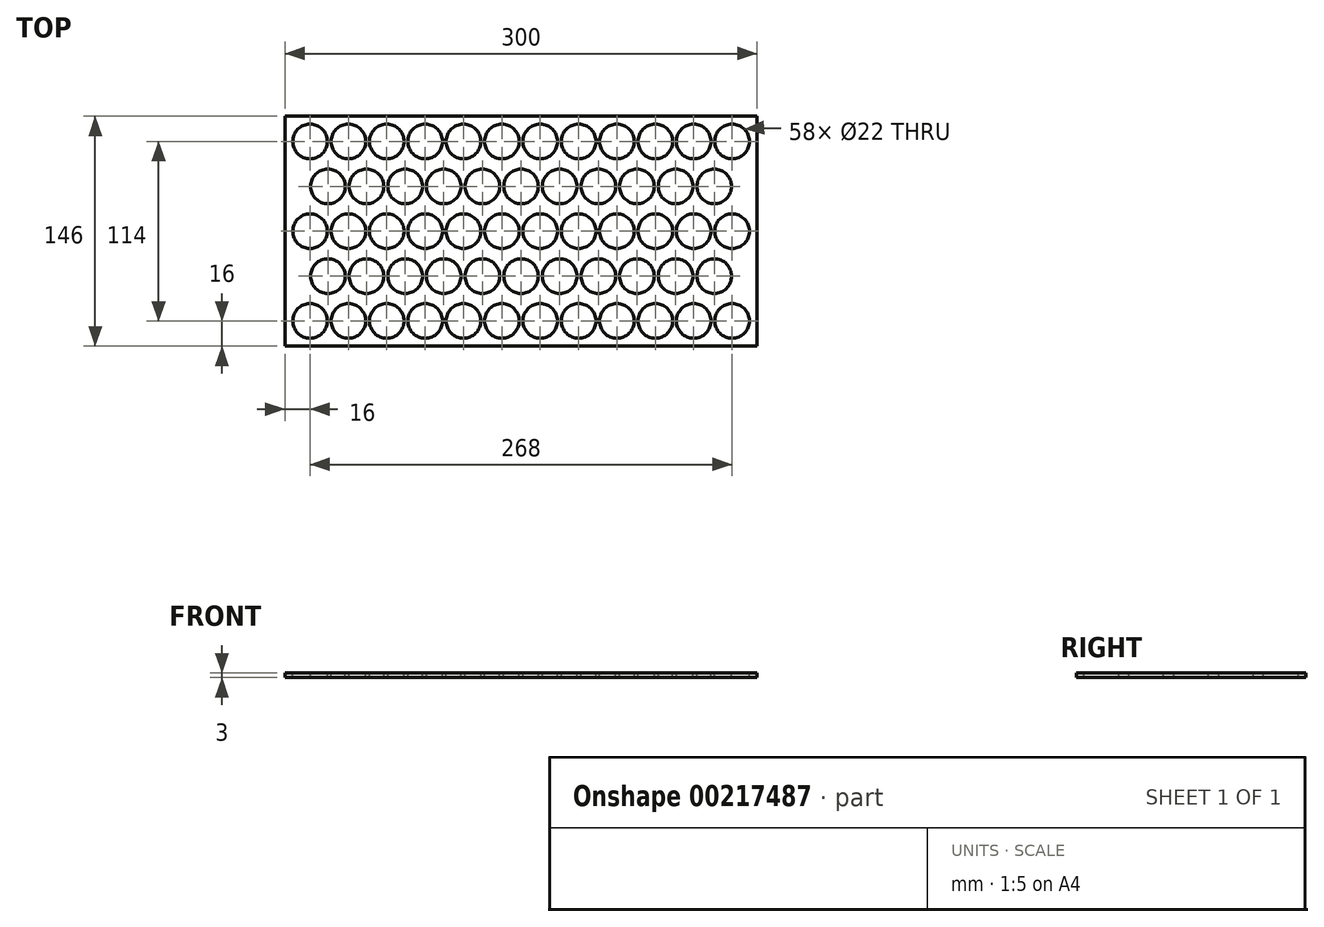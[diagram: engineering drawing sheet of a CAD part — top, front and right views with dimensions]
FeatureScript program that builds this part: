
annotation { "Feature Type Name" : "Feature", "Feature Type Description" : "" }
export const myFeature = defineFeature(function(context is Context, id is Id, definition is map)
    precondition{}
    {
        {
            var Q0;
            Q0=qCreatedBy(makeId("Top.planeOp"),FACE);
            var sketch = newSketch(context, id + "F0", { "sketchPlane" : qUnion([Q0])});
            skLineSegment(sketch, "E0.bottom", {"start": v(0, 0) * mm, "end": v(300, 0) * mm});
            skLineSegment(sketch, "E0.top", {"start": v(0, 146) * mm, "end": v(300, 146) * mm});
            skLineSegment(sketch, "E0.left", {"start": v(0, 0) * mm, "end": v(0, 146) * mm});
            skLineSegment(sketch, "E0.right", {"start": v(300, 0) * mm, "end": v(300, 146) * mm});
            skSolve(sketch);
        }
        {
            var Q0;
            Q0=makeQuery(id+"F0.imprint","IMPRINT",FACE,{"disambiguationData":[TD([[makeQuery(id+"F0.imprint","IMPRINT",EDGE,{"derivedFrom":sQuery(id+"F0.wireOp",EDGE,"E0.bottom")}),1.0]])]});
            extrude(context, id + "F1", {"entities" : qUnion([Q0]), "depth" : 3 * mm});
        }
        {
            var Q0;
            Q0=makeQuery(id+"F1.opExtrude","CAP_FACE",FACE,{"disambiguationData":[OSD([sQuery(id+"F0.wireOp",EDGE,"E0.bottom"),sQuery(id+"F0.wireOp",EDGE,"E0.top"),sQuery(id+"F0.wireOp",EDGE,"E0.left"),sQuery(id+"F0.wireOp",EDGE,"E0.right")])],"isStart":false});
            var sketch = newSketch(context, id + "F2", { "sketchPlane" : qUnion([Q0])});
            skCircle(sketch, "E1", {"center": v(16, 130) * mm, "radius": 11 * mm});
            skCircle(sketch, "E2.1.0.0", {"center": v(40.36, 130) * mm, "radius": 11 * mm});
            skCircle(sketch, "E2.2.0.0", {"center": v(64.73, 130) * mm, "radius": 11 * mm});
            skCircle(sketch, "E2.3.0.0", {"center": v(89.1, 130) * mm, "radius": 11 * mm});
            skCircle(sketch, "E2.4.0.0", {"center": v(113.45, 130) * mm, "radius": 11 * mm});
            skCircle(sketch, "E2.5.0.0", {"center": v(137.82, 130) * mm, "radius": 11 * mm});
            skCircle(sketch, "E2.6.0.0", {"center": v(162.18, 130) * mm, "radius": 11 * mm});
            skCircle(sketch, "E2.7.0.0", {"center": v(186.55, 130) * mm, "radius": 11 * mm});
            skCircle(sketch, "E2.8.0.0", {"center": v(210.9, 130) * mm, "radius": 11 * mm});
            skCircle(sketch, "E2.9.0.0", {"center": v(235.27, 130) * mm, "radius": 11 * mm});
            skCircle(sketch, "E2.10.0.0", {"center": v(259.64, 130) * mm, "radius": 11 * mm});
            skCircle(sketch, "E2.11.0.0", {"center": v(284, 130) * mm, "radius": 11 * mm});
            skLineSegment(sketch, "E2.direction1", {"start": v(16, 130) * mm, "end": v(40.36, 130) * mm, "construction": true});
            skCircle(sketch, "E3.0.1.0", {"center": v(16, 73) * mm, "radius": 11 * mm});
            skCircle(sketch, "E3.0.1.1", {"center": v(40.36, 73) * mm, "radius": 11 * mm});
            skCircle(sketch, "E3.0.1.2", {"center": v(64.73, 73) * mm, "radius": 11 * mm});
            skCircle(sketch, "E3.0.1.3", {"center": v(89.1, 73) * mm, "radius": 11 * mm});
            skCircle(sketch, "E3.0.1.4", {"center": v(113.45, 73) * mm, "radius": 11 * mm});
            skCircle(sketch, "E3.0.1.5", {"center": v(137.82, 73) * mm, "radius": 11 * mm});
            skCircle(sketch, "E3.0.1.6", {"center": v(162.18, 73) * mm, "radius": 11 * mm});
            skCircle(sketch, "E3.0.1.7", {"center": v(186.55, 73) * mm, "radius": 11 * mm});
            skCircle(sketch, "E3.0.1.8", {"center": v(210.9, 73) * mm, "radius": 11 * mm});
            skCircle(sketch, "E3.0.1.9", {"center": v(235.27, 73) * mm, "radius": 11 * mm});
            skCircle(sketch, "E3.0.1.10", {"center": v(259.64, 73) * mm, "radius": 11 * mm});
            skCircle(sketch, "E3.0.1.11", {"center": v(284, 73) * mm, "radius": 11 * mm});
            skCircle(sketch, "E3.0.2.0", {"center": v(16, 16) * mm, "radius": 11 * mm});
            skCircle(sketch, "E3.0.2.1", {"center": v(40.36, 16) * mm, "radius": 11 * mm});
            skCircle(sketch, "E3.0.2.2", {"center": v(64.73, 16) * mm, "radius": 11 * mm});
            skCircle(sketch, "E3.0.2.3", {"center": v(89.1, 16) * mm, "radius": 11 * mm});
            skCircle(sketch, "E3.0.2.4", {"center": v(113.45, 16) * mm, "radius": 11 * mm});
            skCircle(sketch, "E3.0.2.5", {"center": v(137.82, 16) * mm, "radius": 11 * mm});
            skCircle(sketch, "E3.0.2.6", {"center": v(162.18, 16) * mm, "radius": 11 * mm});
            skCircle(sketch, "E3.0.2.7", {"center": v(186.55, 16) * mm, "radius": 11 * mm});
            skCircle(sketch, "E3.0.2.8", {"center": v(210.9, 16) * mm, "radius": 11 * mm});
            skCircle(sketch, "E3.0.2.9", {"center": v(235.27, 16) * mm, "radius": 11 * mm});
            skCircle(sketch, "E3.0.2.10", {"center": v(259.64, 16) * mm, "radius": 11 * mm});
            skCircle(sketch, "E3.0.2.11", {"center": v(284, 16) * mm, "radius": 11 * mm});
            skLineSegment(sketch, "E3.direction1", {"start": v(16, 130) * mm, "end": v(40, 130) * mm, "construction": true});
            skLineSegment(sketch, "E3.direction2", {"start": v(16, 130) * mm, "end": v(16, 73) * mm, "construction": true});
            skCircle(sketch, "E4", {"center": v(27.3, 101.5) * mm, "radius": 11 * mm});
            skPoint(sketch, "E5.startSnap0", {"position": v(16, 101.5) * mm});
            skLineSegment(sketch, "E6", {"start": v(0, 101.5) * mm, "end": v(300, 101.5) * mm, "construction": true});
            skLineSegment(sketch, "E7", {"start": v(0, 44.5) * mm, "end": v(300, 44.5) * mm, "construction": true});
            skCircle(sketch, "E8.0.1.0", {"center": v(27.3, 44.5) * mm, "radius": 11 * mm});
            skCircle(sketch, "E8.1.0.0", {"center": v(51.84, 101.5) * mm, "radius": 11 * mm});
            skCircle(sketch, "E8.1.1.0", {"center": v(51.84, 44.5) * mm, "radius": 11 * mm});
            skCircle(sketch, "E8.2.0.0", {"center": v(76.38, 101.5) * mm, "radius": 11 * mm});
            skCircle(sketch, "E8.2.1.0", {"center": v(76.38, 44.5) * mm, "radius": 11 * mm});
            skCircle(sketch, "E8.3.0.0", {"center": v(100.92, 101.5) * mm, "radius": 11 * mm});
            skCircle(sketch, "E8.3.1.0", {"center": v(100.92, 44.5) * mm, "radius": 11 * mm});
            skCircle(sketch, "E8.4.0.0", {"center": v(125.46, 101.5) * mm, "radius": 11 * mm});
            skCircle(sketch, "E8.4.1.0", {"center": v(125.46, 44.5) * mm, "radius": 11 * mm});
            skCircle(sketch, "E8.5.0.0", {"center": v(150, 101.5) * mm, "radius": 11 * mm});
            skCircle(sketch, "E8.5.1.0", {"center": v(150, 44.5) * mm, "radius": 11 * mm});
            skCircle(sketch, "E8.6.0.0", {"center": v(174.54, 101.5) * mm, "radius": 11 * mm});
            skCircle(sketch, "E8.6.1.0", {"center": v(174.54, 44.5) * mm, "radius": 11 * mm});
            skCircle(sketch, "E8.7.0.0", {"center": v(199.08, 101.5) * mm, "radius": 11 * mm});
            skCircle(sketch, "E8.7.1.0", {"center": v(199.08, 44.5) * mm, "radius": 11 * mm});
            skCircle(sketch, "E8.8.0.0", {"center": v(223.62, 101.5) * mm, "radius": 11 * mm});
            skCircle(sketch, "E8.8.1.0", {"center": v(223.62, 44.5) * mm, "radius": 11 * mm});
            skCircle(sketch, "E8.9.0.0", {"center": v(248.16, 101.5) * mm, "radius": 11 * mm});
            skCircle(sketch, "E8.9.1.0", {"center": v(248.16, 44.5) * mm, "radius": 11 * mm});
            skCircle(sketch, "E8.10.0.0", {"center": v(272.7, 101.5) * mm, "radius": 11 * mm});
            skCircle(sketch, "E8.10.1.0", {"center": v(272.7, 44.5) * mm, "radius": 11 * mm});
            skLineSegment(sketch, "E8.direction1", {"start": v(27.3, 101.5) * mm, "end": v(51.84, 101.5) * mm, "construction": true});
            skLineSegment(sketch, "E8.direction2", {"start": v(27.3, 101.5) * mm, "end": v(27.3, 44.5) * mm, "construction": true});
            skSolve(sketch);
        }
        {
            var Q0;
            Q0 = qSketchRegion(id + "F2", true);
            extrude(context, id + "F3", {"entities" : qUnion([Q0]), "operationType" : NewBodyOperationType.REMOVE, "endBound" : BoundingType.THROUGH_ALL, "oppositeDirection" : true, "depth" : 25 * mm});
        }
    });
